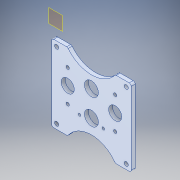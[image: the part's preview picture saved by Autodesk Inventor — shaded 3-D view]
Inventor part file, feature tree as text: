
AUTODESK INVENTOR PART (.ipt)
format: ipt  version: 2018 (Build 220112000, 112)  size: 222,208 bytes
history: native  units: in
note: dims shown in document units (in); Inventor stores cm internally (conversion verified against a paired STEP export)
features: extrude x2, fillet x2, sketch x2, plane x1
ambient origin geometry x8: Origin, YZ Plane, XZ Plane, XY Plane, X Axis, Y Axis, Z Axis, Center Point
bodies: Body1 (feature_tree)
feature tree (7):
  plane  "Work Plane1"
  extrude  "Extrusion1"  Depth=0.25in
  fillet  "Fillet1"  Radius=0.25in
  extrude  "Extrusion2"  Depth=0.125in
  fillet  "Fillet2"  Radius=3.0in
  sketch  "Sketch2"  dims[d0=1.5in d1=1.0in d12=0.25in d13=0.0in]
  sketch  "Sketch5"  dims[d15=0.125in d16=1.5in d17=3.0in d18=0.8in d19=0.75in d20=1.0in d21=0.0in d23=0.312in d24=0.312in d25=0.7in d27=1.506in d29=0.312in d30=0.312in d31=1.706in d33=0.125in]
